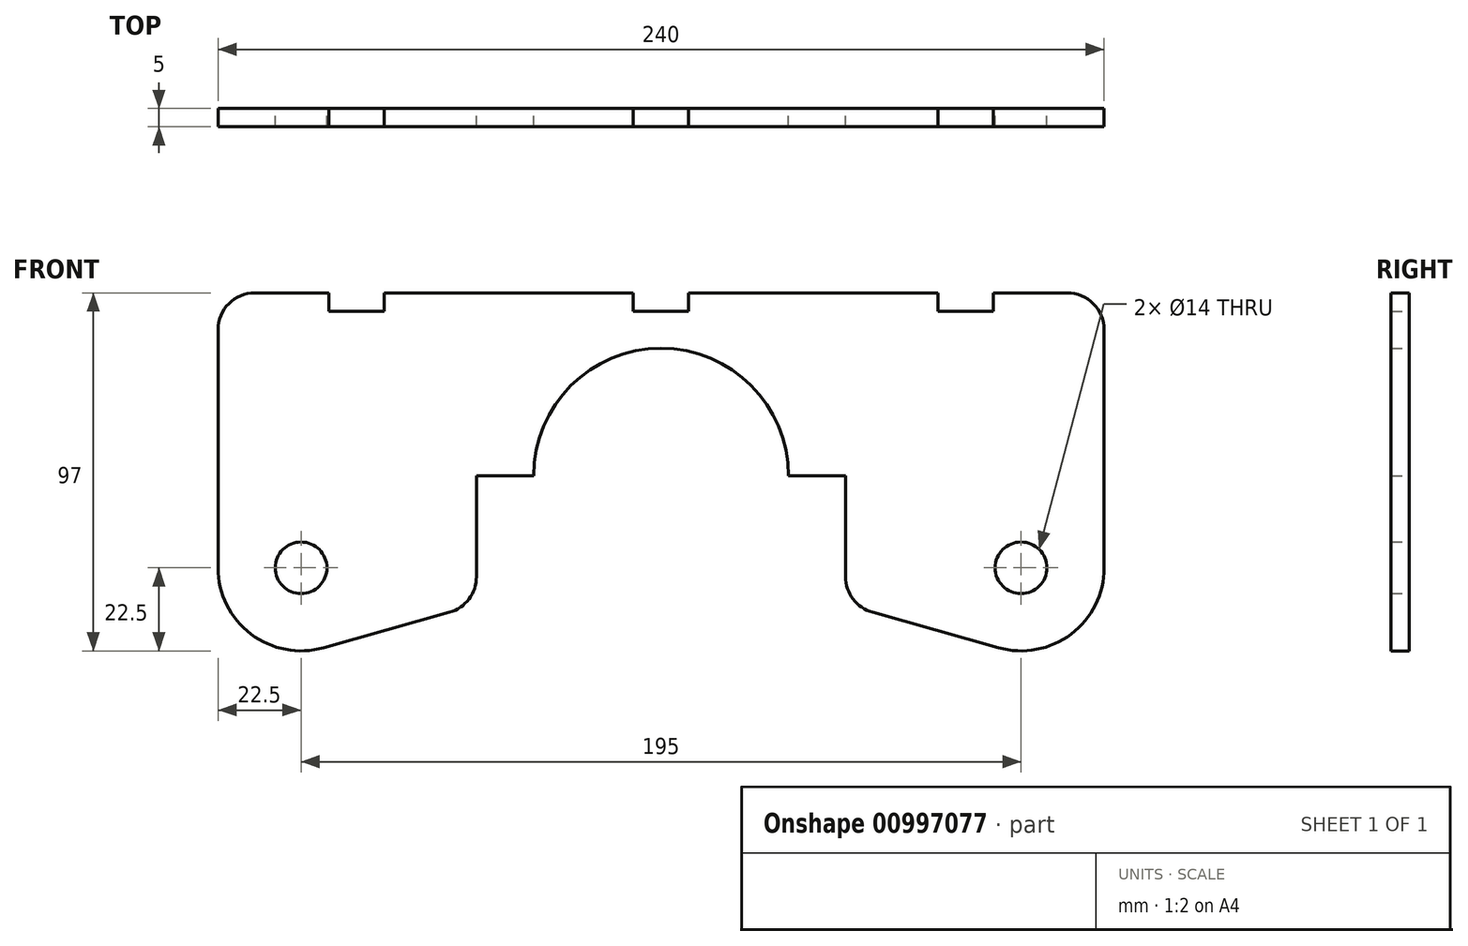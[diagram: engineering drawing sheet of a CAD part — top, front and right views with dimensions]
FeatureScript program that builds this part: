
annotation { "Feature Type Name" : "Feature", "Feature Type Description" : "" }
export const myFeature = defineFeature(function(context is Context, id is Id, definition is map)
    precondition{}
    {
        {
            var Q0;
            Q0=qCreatedBy(makeId("Front.planeOp"),FACE);
            var sketch = newSketch(context, id + "F0", { "sketchPlane" : qUnion([Q0])});
            skCircle(sketch, "E0", {"center": v(-97.5, -25) * mm, "radius": 7 * mm});
            skCircle(sketch, "E1", {"center": v(97.5, -25) * mm, "radius": 7 * mm});
            skArc(sketch, "E2", {"start": v(34.5, 0) * mm, "mid": v(0, 34.5) * mm, "end": v(-34.5, 0) * mm});
            skArc(sketch, "E3", {"start": v(-120, -25) * mm, "mid": v(-111.08, -42.94) * mm, "end": v(-91.4, -46.66) * mm});
            skArc(sketch, "E4", {"start": v(91.4, -46.66) * mm, "mid": v(111.08, -42.94) * mm, "end": v(120, -25) * mm});
            skLineSegment(sketch, "E5", {"start": v(120, -25) * mm, "end": v(120, 39.5) * mm});
            skLineSegment(sketch, "E6", {"start": v(110, 49.5) * mm, "end": v(90, 49.5) * mm});
            skLineSegment(sketch, "E7", {"start": v(-120, 39.5) * mm, "end": v(-120, -25) * mm});
            skLineSegment(sketch, "E8", {"start": v(-34.5, 0) * mm, "end": v(-50, 0) * mm});
            skLineSegment(sketch, "E9", {"start": v(34.5, 0) * mm, "end": v(50, 0) * mm});
            skLineSegment(sketch, "E10", {"start": v(-50, 0) * mm, "end": v(-50, -27.43) * mm});
            skLineSegment(sketch, "E11", {"start": v(-57.29, -37.05) * mm, "end": v(-91.4, -46.66) * mm});
            skLineSegment(sketch, "E12", {"start": v(50, 0) * mm, "end": v(50, -27.43) * mm});
            skLineSegment(sketch, "E13", {"start": v(57.29, -37.05) * mm, "end": v(91.4, -46.66) * mm});
            skPoint(sketch, "E14.visualSharp", {"position": v(-50, -35) * mm});
            skArc(sketch, "E14.filletArc", {"start": v(-57.29, -37.05) * mm, "mid": v(-52.03, -33.46) * mm, "end": v(-50, -27.43) * mm});
            skPoint(sketch, "E15.visualSharp", {"position": v(50, -35) * mm});
            skArc(sketch, "E15.filletArc", {"start": v(50, -27.43) * mm, "mid": v(52.03, -33.46) * mm, "end": v(57.29, -37.05) * mm});
            skPoint(sketch, "E16.visualSharp", {"position": v(-120, 49.5) * mm});
            skArc(sketch, "E16.filletArc", {"start": v(-110, 49.5) * mm, "mid": v(-117.07, 46.57) * mm, "end": v(-120, 39.5) * mm});
            skPoint(sketch, "E17.visualSharp", {"position": v(120, 49.5) * mm});
            skArc(sketch, "E17.filletArc", {"start": v(120, 39.5) * mm, "mid": v(117.07, 46.57) * mm, "end": v(110, 49.5) * mm});
            skLineSegment(sketch, "E18.top", {"start": v(-90, 44.5) * mm, "end": v(-75, 44.5) * mm});
            skLineSegment(sketch, "E18.left", {"start": v(-90, 49.5) * mm, "end": v(-90, 44.5) * mm});
            skLineSegment(sketch, "E18.right", {"start": v(-75, 49.5) * mm, "end": v(-75, 44.5) * mm});
            skLineSegment(sketch, "E19.top", {"start": v(-7.5, 44.5) * mm, "end": v(7.5, 44.5) * mm});
            skLineSegment(sketch, "E19.left", {"start": v(-7.5, 49.5) * mm, "end": v(-7.5, 44.5) * mm});
            skLineSegment(sketch, "E19.right", {"start": v(7.5, 49.5) * mm, "end": v(7.5, 44.5) * mm});
            skLineSegment(sketch, "E20.top", {"start": v(75, 44.5) * mm, "end": v(90, 44.5) * mm});
            skLineSegment(sketch, "E20.left", {"start": v(75, 49.5) * mm, "end": v(75, 44.5) * mm});
            skLineSegment(sketch, "E20.right", {"start": v(90, 49.5) * mm, "end": v(90, 44.5) * mm});
            skLineSegment(sketch, "E21.trimOffspring", {"start": v(-90, 49.5) * mm, "end": v(-110, 49.5) * mm});
            skLineSegment(sketch, "E22.trimOffspring", {"start": v(-7.5, 49.5) * mm, "end": v(-75, 49.5) * mm});
            skLineSegment(sketch, "E23.trimOffspring", {"start": v(75, 49.5) * mm, "end": v(7.5, 49.5) * mm});
            skPoint(sketch, "E24", {"position": v(0, 44.5) * mm});
            skSolve(sketch);
        }
        {
            var Q0;
            Q0 = qSketchRegion(id + "F0", true);
            extrude(context, id + "F1", {"entities" : qUnion([Q0]), "depth" : 5 * mm, "offsetDistance" : 25 * mm});
        }
    });
